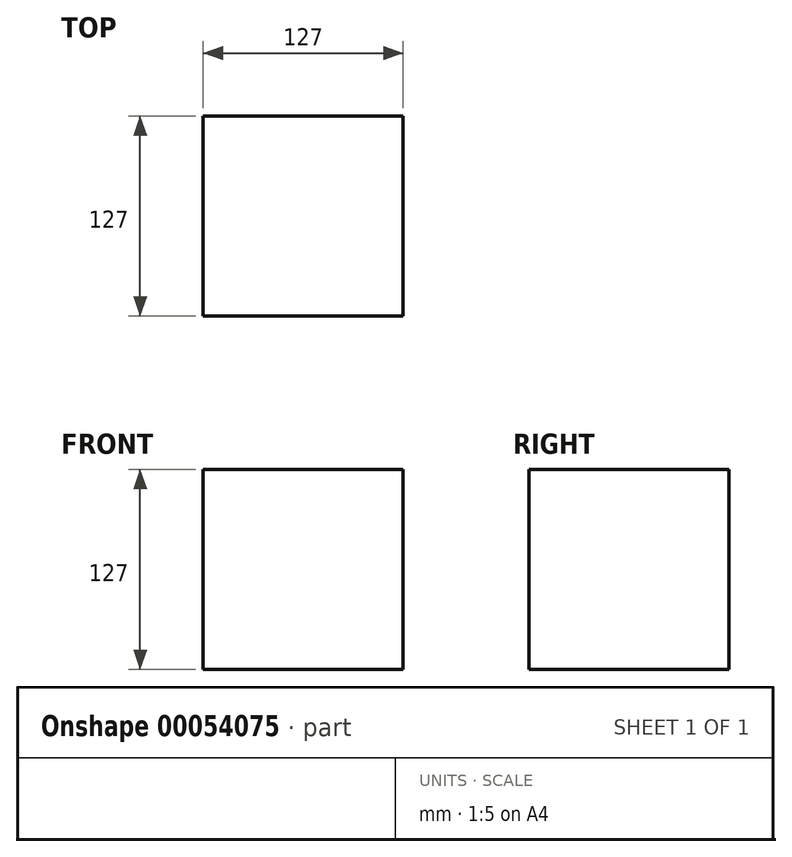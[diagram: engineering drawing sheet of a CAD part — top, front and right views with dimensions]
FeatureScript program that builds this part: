
annotation { "Feature Type Name" : "Feature", "Feature Type Description" : "" }
export const myFeature = defineFeature(function(context is Context, id is Id, definition is map)
    precondition{}
    {
        {
            var Q0;
            Q0=qCreatedBy(makeId("Top.planeOp"),FACE);
            var sketch = newSketch(context, id + "F0", { "sketchPlane" : qUnion([Q0])});
            skLineSegment(sketch, "E0.bottom", {"start": v(0, 0) * mm, "end": v(127, 0) * mm});
            skLineSegment(sketch, "E0.top", {"start": v(0, 127) * mm, "end": v(127, 127) * mm});
            skLineSegment(sketch, "E0.left", {"start": v(0, 0) * mm, "end": v(0, 127) * mm});
            skLineSegment(sketch, "E0.right", {"start": v(127, 0) * mm, "end": v(127, 127) * mm});
            skLineSegment(sketch, "E1", {"start": v(127, 127) * mm, "end": v(0, 0) * mm, "construction": true});
            skCircle(sketch, "E2", {"center": v(63.5, 63.5) * mm, "radius": 50.8 * mm});
            skSolve(sketch);
        }
        {
            var Q0;
            Q0 = qSketchRegion(id + "F0", true);
            var Q1;
            Q1=makeQuery(id+"F0.imprint","IMPRINT",FACE,{"disambiguationData":[TD([[makeQuery(id+"F0.imprint","IMPRINT",EDGE,{"derivedFrom":sQuery(id+"F0.wireOp",EDGE,"E2")}),1.0]])]});
            extrude(context, id + "F1", {"entities" : qUnion([Q0, Q1]), "depth" : 127 * mm});
        }
    });
